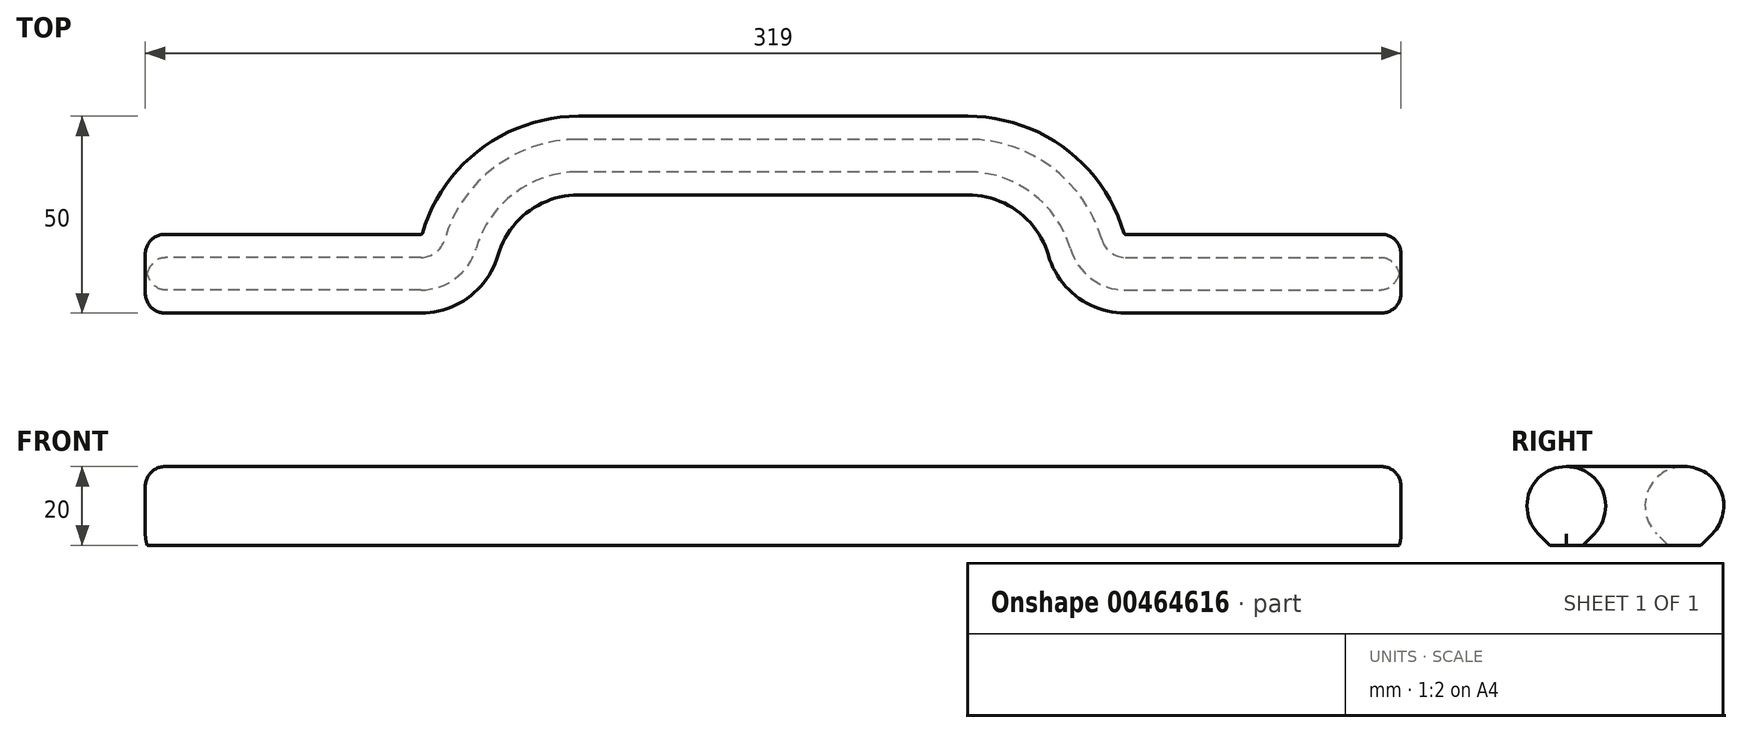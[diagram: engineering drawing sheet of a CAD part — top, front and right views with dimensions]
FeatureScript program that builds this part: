
annotation { "Feature Type Name" : "Feature", "Feature Type Description" : "" }
export const myFeature = defineFeature(function(context is Context, id is Id, definition is map)
    precondition{}
    {
        {
            var Q0;
            Q0=qCreatedBy(makeId("Top.planeOp"),FACE);
            var sketch = newSketch(context, id + "F0", { "sketchPlane" : qUnion([Q0])});
            skLineSegment(sketch, "E0.bottom", {"start": v(-159.5, 66) * mm, "end": v(159.5, 66) * mm, "construction": true});
            skLineSegment(sketch, "E0.top", {"start": v(-159.5, -66) * mm, "end": v(159.5, -66) * mm, "construction": true});
            skLineSegment(sketch, "E0.left", {"start": v(-159.5, 66) * mm, "end": v(-159.5, -66) * mm, "construction": true});
            skLineSegment(sketch, "E0.right", {"start": v(159.5, 66) * mm, "end": v(159.5, -66) * mm, "construction": true});
            skPoint(sketch, "E0.middle", {"position": v(0, 0) * mm});
            skLineSegment(sketch, "E1", {"start": v(-159.5, -30) * mm, "end": v(-89.5, -30) * mm});
            skLineSegment(sketch, "E2", {"start": v(0, 0) * mm, "end": v(0, 66) * mm, "construction": true});
            skLineSegment(sketch, "E3", {"start": v(0, 0) * mm, "end": v(-49.5, 0) * mm});
            skArc(sketch, "E4", {"start": v(-49.5, 0) * mm, "mid": v(-68.25, -6.25) * mm, "end": v(-79.5, -22.5) * mm});
            skArc(sketch, "E5", {"start": v(-89.5, -30) * mm, "mid": v(-83.25, -27.92) * mm, "end": v(-79.5, -22.5) * mm});
            skSolve(sketch);
        }
        {
            var Q0;
            Q0=qCreatedBy(makeId("Right.planeOp"),FACE);
            var sketch = newSketch(context, id + "F1", { "sketchPlane" : qUnion([Q0])});
            skCircle(sketch, "E6", {"center": v(0, 10) * mm, "radius": 10 * mm});
            skLineSegment(sketch, "E7", {"start": v(0, 0) * mm, "end": v(-4.14, 0) * mm});
            skLineSegment(sketch, "E8", {"start": v(-4.14, 0) * mm, "end": v(-7.07, 2.93) * mm});
            skLineSegment(sketch, "E9", {"start": v(0, 0) * mm, "end": v(0, 10) * mm, "construction": true});
            skLineSegment(sketch, "E10.MirrorCS", {"start": v(4.14, 0) * mm, "end": v(7.07, 2.93) * mm});
            skLineSegment(sketch, "E11.MirrorCS", {"start": v(0, 0) * mm, "end": v(4.14, 0) * mm});
            skSolve(sketch);
        }
        {
            var Q0;
            {var subQ0=sQuery(id+"F1.wireOp",EDGE,"E6");var subQ2=makeQuery(id+"F1.imprint","INTERSECT",VERTEX,{"derivedFrom":[subQ0,sQuery(id+"F1.wireOp",EDGE,"E8")]});Q0=makeQuery(id+"F1.imprint","IMPRINT",FACE,{"disambiguationData":[TD([[makeQuery(id+"F1.imprint","IMPRINT",EDGE,{"disambiguationData":[TD([[subQ2,1.0]])],"derivedFrom":subQ0}),1.0]])]});}
            var Q1;
            {var subQ0=sQuery(id+"F1.wireOp",EDGE,"E7");Q1=makeQuery(id+"F1.imprint","IMPRINT",FACE,{"disambiguationData":[TD([[makeQuery(id+"F1.imprint","IMPRINT",EDGE,{"derivedFrom":subQ0}),-1.0]])]});}
            var Q2;
            {var subQ2=sQuery(id+"F1.wireOp",EDGE,"E10.MirrorCS");Q2=makeQuery(id+"F1.imprint","IMPRINT",FACE,{"disambiguationData":[TD([[makeQuery(id+"F1.imprint","IMPRINT",EDGE,{"derivedFrom":subQ2}),1.0]])]});}
            var Q3;
            Q3=sQuery(id+"F0.wireOp",EDGE,"E3");
            var Q4;
            Q4=sQuery(id+"F0.wireOp",EDGE,"E4");
            var Q5;
            Q5=sQuery(id+"F0.wireOp",EDGE,"E5");
            var Q6;
            Q6=sQuery(id+"F0.wireOp",EDGE,"E1");
            sweep(context, id + "F2", {"profiles" : qUnion([Q0, Q1, Q2]), "path" : qUnion([Q3, Q4, Q5, Q6])});
        }
        {
            var Q0;
            Q0=makeQuery(id+"F2.opSweep","SWEPT_BODY",BODY,{"disambiguationData":[OSD([sQuery(id+"F0.wireOp",EDGE,"E1"),sQuery(id+"F1.wireOp",EDGE,"E6"),sQuery(id+"F1.wireOp",EDGE,"E7"),sQuery(id+"F1.wireOp",EDGE,"E8"),sQuery(id+"F1.wireOp",EDGE,"E10.MirrorCS"),sQuery(id+"F1.wireOp",EDGE,"E11.MirrorCS")])]});
            var Q1;
            Q1=qCreatedBy(makeId("Right.planeOp"),FACE);
            mirror(context, id + "F3", {"operationType" : NewBodyOperationType.ADD, "entities" : qUnion([Q0]), "mirrorPlane" : qUnion([Q1])});
        }
        {
            var Q0;
            Q0=makeQuery(id+"F2.opSweep","CAP_EDGE",EDGE,{"disambiguationData":[OSD([sQuery(id+"F0.wireOp",VERTEX,"E1.start"),sQuery(id+"F1.wireOp",EDGE,"E6")])],"isStart":false});
            var Q1;
            Q1=makeQuery(id+"F3.opPattern","COPY",EDGE,{"derivedFrom":makeQuery(id+"F2.opSweep","CAP_EDGE",EDGE,{"disambiguationData":[OSD([sQuery(id+"F0.wireOp",VERTEX,"E1.start"),sQuery(id+"F1.wireOp",EDGE,"E6")])],"isStart":false}),"instanceName":"1"});
            fillet(context, id + "F4", {"entities" : qUnion([Q0, Q1]), "radius" : 5 * mm, "tangentPropagation" : true, "allowEdgeOverflow" : false});
        }
    });
